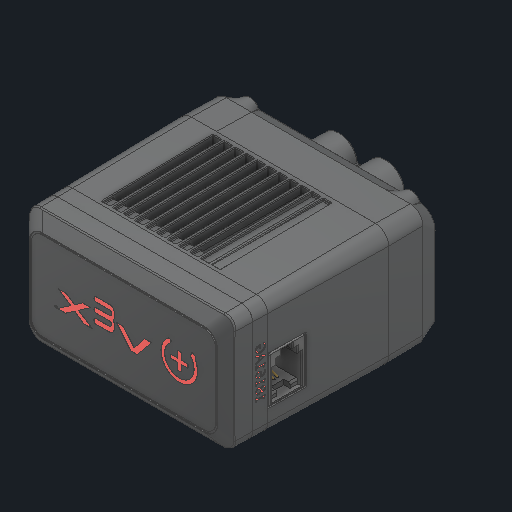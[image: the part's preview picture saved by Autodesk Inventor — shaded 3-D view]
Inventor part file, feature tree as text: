
AUTODESK INVENTOR PART (.ipt)
format: ipt  version: 2024 (Build 280153000, 153)  size: 13,049,344 bytes
history: native  units: in
note: dims shown in document units (in); Inventor stores cm internally (conversion verified against a paired STEP export)
features: other x19, sketch x2
ambient origin geometry x8: Origin, YZ Plane, XZ Plane, XY Plane, X Axis, Y Axis, Z Axis, Center Point
bodies: Solid1 (feature_tree), Solid2 (feature_tree), Solid7 (feature_tree), Solid8 (feature_tree), Solid9 (feature_tree), Solid20 (feature_tree), Solid21 (feature_tree), Solid22 (feature_tree)
feature tree (21):
  other  "V5 Motor.ipt"
  other  "Solid1::V5 Motor.ipt"
  other  "Solid2::V5 Motor.ipt"
  other  "Solid4::V5 Motor.ipt"
  other  "Solid6::V5 Motor.ipt"
  other  "Solid7::V5 Motor.ipt"
  other  "Solid8::V5 Motor.ipt"
  other  "Solid9::V5 Motor.ipt"
  other  "Solid14::V5 Motor.ipt"
  other  "Solid16::V5 Motor.ipt"
  other  "Solid17::V5 Motor.ipt"
  other  "Solid18::V5 Motor.ipt"
  other  "Solid19::V5 Motor.ipt"
  other  "Solid20::V5 Motor.ipt"
  other  "Solid21::V5 Motor.ipt"
  other  "Solid22::V5 Motor.ipt"
  other  "TaggingFeature1"
  sketch  "Sketch1"  dims[d0=0.3937in]
  sketch  "Sketch2"  dims[d4=0.0in d5=0.0in]
  other  "iInsert:1"
  other  "iInsert:2"
